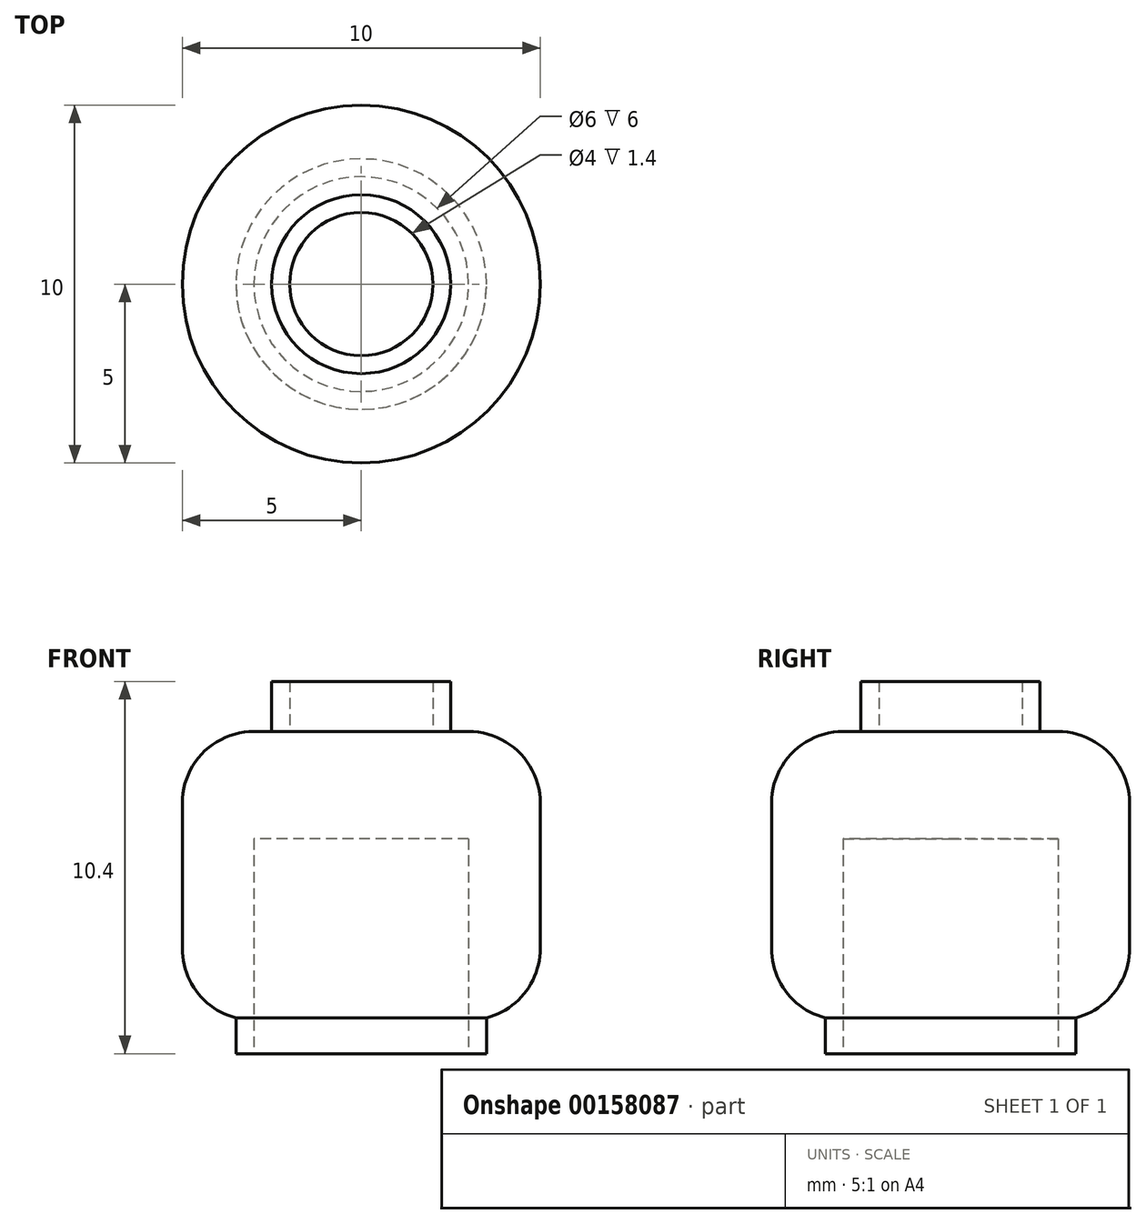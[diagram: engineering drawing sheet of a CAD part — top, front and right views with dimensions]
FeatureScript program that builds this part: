
annotation { "Feature Type Name" : "Feature", "Feature Type Description" : "" }
export const myFeature = defineFeature(function(context is Context, id is Id, definition is map)
    precondition{}
    {
        {
            var Q0;
            Q0=qCreatedBy(makeId("Top.planeOp"),FACE);
            var sketch = newSketch(context, id + "F0", { "sketchPlane" : qUnion([Q0])});
            skCircle(sketch, "E0", {"center": v(0, 0) * mm, "radius": 3 * mm});
            skCircle(sketch, "E1", {"center": v(0, 0) * mm, "radius": 3.5 * mm});
            skSolve(sketch);
        }
        {
            var Q0;
            Q0=makeQuery(id+"F0.imprint","IMPRINT",FACE,{"disambiguationData":[TD([[makeQuery(id+"F0.imprint","IMPRINT",EDGE,{"derivedFrom":sQuery(id+"F0.wireOp",EDGE,"E0")}),-1.0]])]});
            extrude(context, id + "F1", {"entities" : qUnion([Q0]), "depth" : 1 * mm});
        }
        {
            var Q0;
            Q0=makeQuery(id+"F1.opExtrude","CAP_FACE",FACE,{"disambiguationData":[OSD([sQuery(id+"F0.wireOp",EDGE,"E0"),sQuery(id+"F0.wireOp",EDGE,"E1")])],"isStart":false});
            var sketch = newSketch(context, id + "F2", { "sketchPlane" : qUnion([Q0])});
            skCircle(sketch, "E2", {"center": v(0, 0) * mm, "radius": 5 * mm});
            skSolve(sketch);
        }
        {
            var Q0;
            Q0=makeQuery(id+"F2.imprint","IMPRINT",FACE,{"disambiguationData":[TD([[makeQuery(id+"F2.imprint","IMPRINT",EDGE,{"derivedFrom":sQuery(id+"F2.wireOp",EDGE,"E2")}),1.0]])]});
            var Q1;
            Q1=makeQuery(id+"F2.imprint","IMPRINT",FACE,{"disambiguationData":[TD([[makeQuery(id+"F2.imprint","IMPRINT",EDGE,{"derivedFrom":makeQuery(id+"F1.opExtrude","CAP_EDGE",EDGE,{"disambiguationData":[OSD([sQuery(id+"F0.wireOp",EDGE,"E0")])],"isStart":false})}),-1.0]])]});
            var Q2;
            Q2=makeQuery(id+"F2.imprint","IMPRINT",FACE,{"disambiguationData":[TD([[makeQuery(id+"F2.imprint","IMPRINT",EDGE,{"derivedFrom":makeQuery(id+"F1.opExtrude","CAP_EDGE",EDGE,{"disambiguationData":[OSD([sQuery(id+"F0.wireOp",EDGE,"E0")])],"isStart":false})}),1.0]])]});
            extrude(context, id + "F3", {"entities" : qUnion([Q0, Q1, Q2]), "operationType" : NewBodyOperationType.ADD, "depth" : 8 * mm});
        }
        {
            var Q0;
            Q0=makeQuery(id+"F3.opExtrude","CAP_FACE",FACE,{"disambiguationData":[OSD([sQuery(id+"F2.wireOp",EDGE,"E2")])],"isStart":false});
            var sketch = newSketch(context, id + "F4", { "sketchPlane" : qUnion([Q0])});
            skCircle(sketch, "E3", {"center": v(0, 0) * mm, "radius": 2.5 * mm});
            skCircle(sketch, "E4", {"center": v(0, 0) * mm, "radius": 2 * mm});
            skSolve(sketch);
        }
        {
            var Q0;
            Q0=makeQuery(id+"F4.imprint","IMPRINT",FACE,{"disambiguationData":[TD([[makeQuery(id+"F4.imprint","IMPRINT",EDGE,{"derivedFrom":sQuery(id+"F4.wireOp",EDGE,"E3")}),1.0]])]});
            extrude(context, id + "F5", {"entities" : qUnion([Q0]), "operationType" : NewBodyOperationType.ADD, "depth" : 1.4 * mm});
        }
        {
            var Q0;
            Q0=makeQuery(id+"F3.opExtrude","CAP_EDGE",EDGE,{"disambiguationData":[OSD([sQuery(id+"F2.wireOp",EDGE,"E2")])],"isStart":false});
            var Q1;
            Q1=makeQuery(id+"F3.opExtrude","CAP_EDGE",EDGE,{"disambiguationData":[OSD([sQuery(id+"F2.wireOp",EDGE,"E2")])],"isStart":true});
            fillet(context, id + "F6", {"entities" : qUnion([Q0, Q1]), "radius" : 2 * mm, "tangentPropagation" : true, "allowEdgeOverflow" : false});
        }
        {
            var Q0;
            Q0=makeQuery(id+"F3.boolean.opBoolean","SPLIT",FACE,{"disambiguationData":[TD([makeQuery(id+"F1.opExtrude","SWEPT_FACE",FACE,{"disambiguationData":[OSD([sQuery(id+"F0.wireOp",EDGE,"E0")])]})])],"derivedFrom":makeQuery(id+"F3.opExtrude","CAP_FACE",FACE,{"disambiguationData":[OSD([sQuery(id+"F2.wireOp",EDGE,"E2")])],"isStart":true})});
            extrude(context, id + "F7", {"entities" : qUnion([Q0]), "operationType" : NewBodyOperationType.REMOVE, "oppositeDirection" : true, "depth" : 5 * mm});
        }
    });
